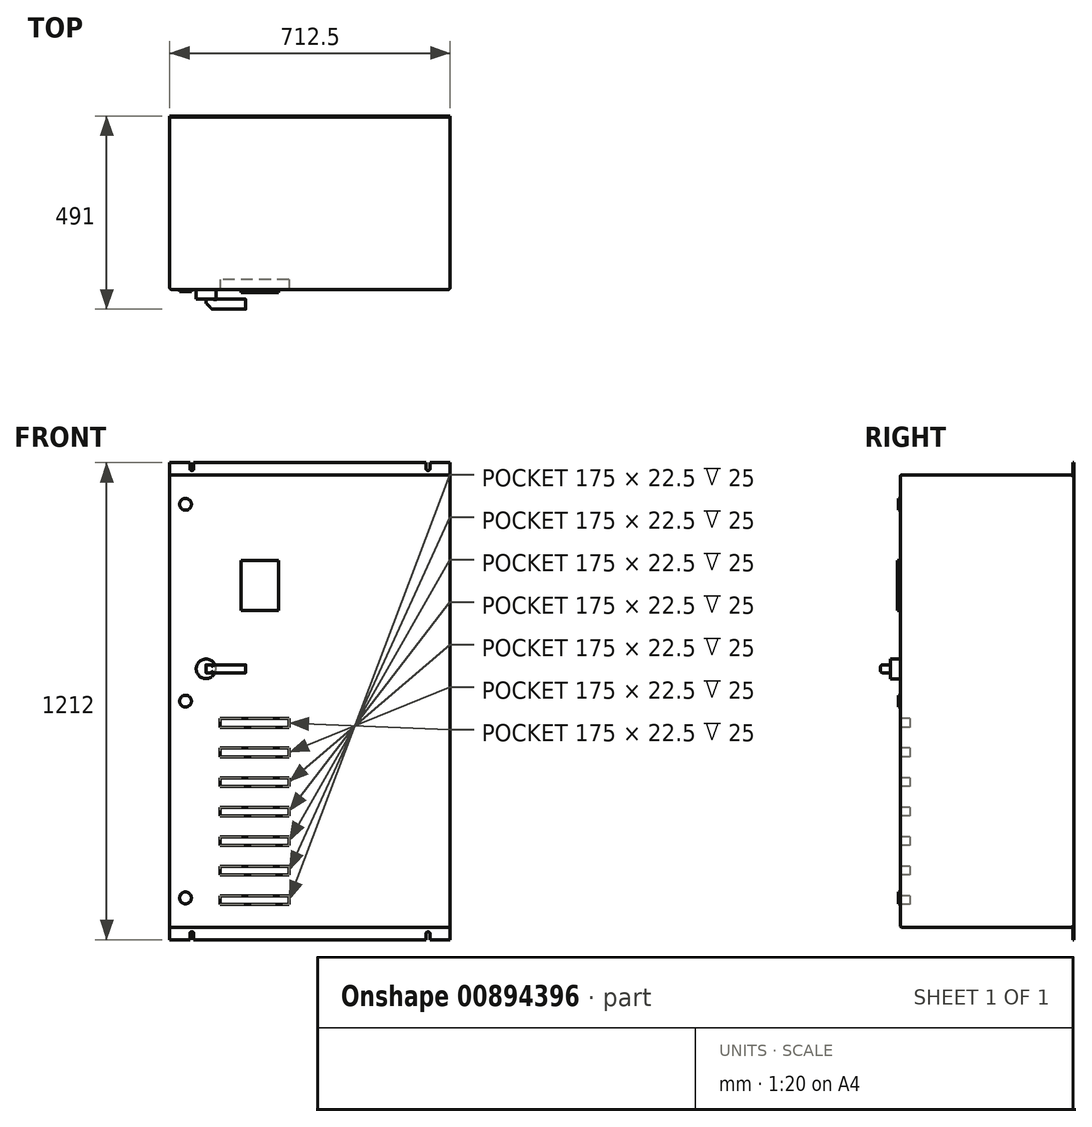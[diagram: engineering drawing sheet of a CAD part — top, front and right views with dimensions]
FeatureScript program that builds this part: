
annotation { "Feature Type Name" : "Feature", "Feature Type Description" : "" }
export const myFeature = defineFeature(function(context is Context, id is Id, definition is map)
    precondition{}
    {
        {
            var Q0;
            Q0=qCreatedBy(makeId("Front.planeOp"),FACE);
            var sketch = newSketch(context, id + "F0", { "sketchPlane" : qUnion([Q0])});
            skLineSegment(sketch, "E0.bottom", {"start": v(356.25, 575) * mm, "end": v(-356.25, 575) * mm});
            skLineSegment(sketch, "E0.top", {"start": v(356.25, -575) * mm, "end": v(-356.25, -575) * mm});
            skLineSegment(sketch, "E0.left", {"start": v(356.25, 575) * mm, "end": v(356.25, -575) * mm});
            skLineSegment(sketch, "E0.right", {"start": v(-356.25, 575) * mm, "end": v(-356.25, -575) * mm});
            skPoint(sketch, "E0.middle", {"position": v(0, 0) * mm});
            skSolve(sketch);
        }
        {
            var Q0;
            Q0 = qSketchRegion(id + "F0", true);
            extrude(context, id + "F1", {"entities" : qUnion([Q0]), "depth" : 438 * mm, "offsetDistance" : 25 * mm});
        }
        {
            var Q0;
            Q0=makeQuery(id+"F1.opExtrude","CAP_FACE",FACE,{"disambiguationData":[OSD([sQuery(id+"F0.wireOp",EDGE,"E0.bottom"),sQuery(id+"F0.wireOp",EDGE,"E0.top"),sQuery(id+"F0.wireOp",EDGE,"E0.left"),sQuery(id+"F0.wireOp",EDGE,"E0.right")])],"isStart":false});
            var sketch = newSketch(context, id + "F2", { "sketchPlane" : qUnion([Q0])});
            skCircle(sketch, "E1", {"center": v(-263.95, 82) * mm, "radius": 25 * mm});
            skSolve(sketch);
        }
        {
            var Q0;
            Q0 = qSketchRegion(id + "F2", true);
            extrude(context, id + "F3", {"entities" : qUnion([Q0]), "depth" : 25 * mm, "offsetDistance" : 25 * mm});
        }
        {
            var Q0;
            Q0=makeQuery(id+"F3.opExtrude","CAP_FACE",FACE,{"disambiguationData":[OSD([sQuery(id+"F2.wireOp",EDGE,"E1")])],"isStart":false});
            var sketch = newSketch(context, id + "F4", { "sketchPlane" : qUnion([Q0])});
            skLineSegment(sketch, "E2", {"start": v(-263.95, 82) * mm, "end": v(-263.95, 92) * mm});
            skLineSegment(sketch, "E3", {"start": v(-263.95, 92) * mm, "end": v(-163.46, 92) * mm});
            skLineSegment(sketch, "E4", {"start": v(-163.46, 92) * mm, "end": v(-163.46, 72) * mm});
            skLineSegment(sketch, "E5", {"start": v(-163.46, 72) * mm, "end": v(-263.95, 72) * mm});
            skLineSegment(sketch, "E6", {"start": v(-263.95, 72) * mm, "end": v(-263.95, 82) * mm});
            skSolve(sketch);
        }
        {
            var Q0;
            Q0 = qSketchRegion(id + "F4", true);
            extrude(context, id + "F5", {"entities" : qUnion([Q0]), "operationType" : NewBodyOperationType.ADD, "depth" : 25 * mm, "offsetDistance" : 25 * mm});
        }
        {
            var Q0;
            Q0=makeQuery(id+"F5.opExtrude","CAP_EDGE",EDGE,{"disambiguationData":[OSD([sQuery(id+"F4.wireOp",EDGE,"E2"),sQuery(id+"F4.wireOp",EDGE,"E6")])],"isStart":false});
            chamfer(context, id + "F6", {"entities" : qUnion([Q0]), "width" : 15 * mm, "tangentPropagation" : true});
        }
        {
            var Q0;
            {var subQ0=sQuery(id+"F4.wireOp",EDGE,"E5");Q0=makeQuery(id+"F5.boolean.opBoolean","SPLIT",EDGE,{"disambiguationData":[topologyDisambiguationEdgeConnected([makeQuery(id+"F3.opExtrude","CAP_FACE",FACE,{"disambiguationData":[OSD([sQuery(id+"F2.wireOp",EDGE,"E1")])],"isStart":false})])],"derivedFrom":makeQuery(id+"F5.opExtrude","CAP_EDGE",EDGE,{"disambiguationData":[OSD([subQ0])],"isStart":true})});}
            var Q1;
            Q1=makeQuery(id+"F5.opExtrude","CAP_EDGE",EDGE,{"disambiguationData":[OSD([sQuery(id+"F4.wireOp",EDGE,"E2"),sQuery(id+"F4.wireOp",EDGE,"E6")])],"isStart":true});
            var Q2;
            {var subQ0=sQuery(id+"F4.wireOp",EDGE,"E3");Q2=makeQuery(id+"F5.boolean.opBoolean","SPLIT",EDGE,{"disambiguationData":[topologyDisambiguationEdgeConnected([makeQuery(id+"F3.opExtrude","CAP_FACE",FACE,{"disambiguationData":[OSD([sQuery(id+"F2.wireOp",EDGE,"E1")])],"isStart":false})])],"derivedFrom":makeQuery(id+"F5.opExtrude","CAP_EDGE",EDGE,{"disambiguationData":[OSD([subQ0])],"isStart":true})});}
            var Q3;
            Q3=makeQuery(id+"F5.opExtrude","CAP_EDGE",EDGE,{"disambiguationData":[OSD([sQuery(id+"F4.wireOp",EDGE,"E3")])],"isStart":false});
            var Q4;
            Q4=makeQuery(id+"F5.opExtrude","CAP_EDGE",EDGE,{"disambiguationData":[OSD([sQuery(id+"F4.wireOp",EDGE,"E5")])],"isStart":false});
            var Q5;
            {var subQ0=sQuery(id+"F4.wireOp",EDGE,"E6");var subQ1=sQuery(id+"F4.wireOp",EDGE,"E2");Q5=makeQuery(id+"F6.opChamfer","BLEND_EDGE",EDGE,{"blendedFrom":[makeQuery(id+"F5.opExtrude","CAP_EDGE",EDGE,{"disambiguationData":[OSD([subQ1,subQ0])],"isStart":false}),makeQuery(id+"F5.opExtrude","CAP_FACE",FACE,{"disambiguationData":[OSD([subQ1,sQuery(id+"F4.wireOp",EDGE,"E3"),sQuery(id+"F4.wireOp",EDGE,"E4"),sQuery(id+"F4.wireOp",EDGE,"E5"),subQ0])],"isStart":false})],"blendedInto":[makeQuery(id+"F5.opExtrude","CAP_FACE",FACE,{"disambiguationData":[OSD([subQ1,sQuery(id+"F4.wireOp",EDGE,"E3"),sQuery(id+"F4.wireOp",EDGE,"E4"),sQuery(id+"F4.wireOp",EDGE,"E5"),subQ0])],"isStart":false})]});}
            var Q6;
            {var subQ0=sQuery(id+"F4.wireOp",EDGE,"E6");var subQ1=sQuery(id+"F4.wireOp",EDGE,"E2");Q6=makeQuery(id+"F6.opChamfer","BLEND_EDGE",EDGE,{"blendedFrom":[makeQuery(id+"F5.opExtrude","CAP_EDGE",EDGE,{"disambiguationData":[OSD([subQ1,subQ0])],"isStart":false}),makeQuery(id+"F5.opExtrude","SWEPT_FACE",FACE,{"disambiguationData":[OSD([subQ1,subQ0])]})],"blendedInto":[makeQuery(id+"F5.opExtrude","SWEPT_FACE",FACE,{"disambiguationData":[OSD([subQ1,subQ0])]})]});}
            fillet(context, id + "F7", {"entities" : qUnion([Q0, Q1, Q2, Q3, Q4, Q5, Q6]), "radius" : 5 * mm, "tangentPropagation" : true, "allowEdgeOverflow" : false});
        }
        {
            var Q0;
            Q0=makeQuery(id+"F1.opExtrude","CAP_FACE",FACE,{"disambiguationData":[OSD([sQuery(id+"F0.wireOp",EDGE,"E0.bottom"),sQuery(id+"F0.wireOp",EDGE,"E0.top"),sQuery(id+"F0.wireOp",EDGE,"E0.left"),sQuery(id+"F0.wireOp",EDGE,"E0.right")])],"isStart":true});
            var sketch = newSketch(context, id + "F8", { "sketchPlane" : qUnion([Q0])});
            skLineSegment(sketch, "E7.bottom", {"start": v(356.25, 606) * mm, "end": v(300, 606) * mm});
            skLineSegment(sketch, "E7.top", {"start": v(356.25, -606) * mm, "end": v(305, -606) * mm});
            skLineSegment(sketch, "E7.left", {"start": v(356.25, 606) * mm, "end": v(356.25, -606) * mm});
            skLineSegment(sketch, "E7.right", {"start": v(-356.25, 606) * mm, "end": v(-356.25, -606) * mm});
            skPoint(sketch, "E7.middle", {"position": v(0, 0) * mm});
            skLineSegment(sketch, "E8", {"start": v(0, 665.64) * mm, "end": v(0, -668.18) * mm, "construction": true});
            skLineSegment(sketch, "E9.bottom", {"start": v(300, 647.98) * mm, "end": v(-300, 647.98) * mm, "construction": true});
            skLineSegment(sketch, "E9.top", {"start": v(300, -647.98) * mm, "end": v(-300, -647.98) * mm, "construction": true});
            skLineSegment(sketch, "E9.left", {"start": v(300, 647.98) * mm, "end": v(300, -647.98) * mm, "construction": true});
            skLineSegment(sketch, "E9.right", {"start": v(-300, 647.98) * mm, "end": v(-300, -647.98) * mm, "construction": true});
            skLineSegment(sketch, "E10.left", {"start": v(-295, -606) * mm, "end": v(-295, -591) * mm});
            skLineSegment(sketch, "E10.right", {"start": v(-305, -606) * mm, "end": v(-305, -591) * mm});
            skPoint(sketch, "E10.middle", {"position": v(-300, -598.5) * mm});
            skArc(sketch, "E11", {"start": v(-305, -591) * mm, "mid": v(-300, -586) * mm, "end": v(-295, -591) * mm});
            skLineSegment(sketch, "E12.trimOffspring", {"start": v(-305, -606) * mm, "end": v(-356.25, -606) * mm});
            skLineSegment(sketch, "E13.MirrorCS", {"start": v(295, -606) * mm, "end": v(300, -606) * mm});
            skLineSegment(sketch, "E14.MirrorCS", {"start": v(305, -606) * mm, "end": v(305, -591) * mm});
            skLineSegment(sketch, "E15.MirrorCS", {"start": v(300, -606) * mm, "end": v(295, -606) * mm});
            skArc(sketch, "E16.MirrorCS", {"start": v(305, -591) * mm, "mid": v(300, -586) * mm, "end": v(295, -591) * mm});
            skLineSegment(sketch, "E17.MirrorCS", {"start": v(295, -606) * mm, "end": v(295, -591) * mm});
            skPoint(sketch, "E18.MirrorP", {"position": v(300, -598.5) * mm});
            skLineSegment(sketch, "E19.MirrorCS", {"start": v(-300, 606) * mm, "end": v(-305, 606) * mm});
            skLineSegment(sketch, "E20.MirrorCS", {"start": v(305, 606) * mm, "end": v(300, 606) * mm});
            skArc(sketch, "E21.MirrorCS", {"start": v(305, 591) * mm, "mid": v(300, 586) * mm, "end": v(295, 591) * mm});
            skLineSegment(sketch, "E22.MirrorCS", {"start": v(295, 606) * mm, "end": v(295, 591) * mm});
            skArc(sketch, "E23.MirrorCS", {"start": v(-305, 591) * mm, "mid": v(-300, 586) * mm, "end": v(-295, 591) * mm});
            skLineSegment(sketch, "E24.MirrorCS", {"start": v(-305, 606) * mm, "end": v(-305, 591) * mm});
            skLineSegment(sketch, "E25.MirrorCS", {"start": v(300, 606) * mm, "end": v(305, 606) * mm});
            skLineSegment(sketch, "E26.MirrorCS", {"start": v(-305, 606) * mm, "end": v(-300, 606) * mm});
            skLineSegment(sketch, "E27.MirrorCS", {"start": v(-295, 606) * mm, "end": v(-295, 591) * mm});
            skLineSegment(sketch, "E28.MirrorCS", {"start": v(305, 606) * mm, "end": v(305, 591) * mm});
            skPoint(sketch, "E29.MirrorP", {"position": v(300, 598.5) * mm});
            skPoint(sketch, "E30.MirrorP", {"position": v(-300, 598.5) * mm});
            skLineSegment(sketch, "E31.trimOffspring", {"start": v(300, -606) * mm, "end": v(-295, -606) * mm});
            skLineSegment(sketch, "E32.trimOffspring", {"start": v(295, 606) * mm, "end": v(-295, 606) * mm});
            skLineSegment(sketch, "E33.trimOffspring", {"start": v(-300, 606) * mm, "end": v(-356.25, 606) * mm});
            skPoint(sketch, "E34.orphan", {"position": v(-295, 606) * mm});
            skSolve(sketch);
        }
        {
            var Q0;
            Q0 = qSketchRegion(id + "F8", true);
            extrude(context, id + "F9", {"entities" : qUnion([Q0]), "operationType" : NewBodyOperationType.ADD, "depth" : 3 * mm, "offsetDistance" : 25 * mm});
        }
        {
            var Q0;
            Q0=makeQuery(id+"F1.opExtrude","CAP_FACE",FACE,{"disambiguationData":[OSD([sQuery(id+"F0.wireOp",EDGE,"E0.bottom"),sQuery(id+"F0.wireOp",EDGE,"E0.top"),sQuery(id+"F0.wireOp",EDGE,"E0.left"),sQuery(id+"F0.wireOp",EDGE,"E0.right")])],"isStart":false});
            var sketch = newSketch(context, id + "F10", { "sketchPlane" : qUnion([Q0])});
            skLineSegment(sketch, "E35.bottom", {"start": v(-79.36, 357.66) * mm, "end": v(-175.27, 357.66) * mm});
            skLineSegment(sketch, "E35.top", {"start": v(-79.36, 230.17) * mm, "end": v(-175.27, 230.17) * mm});
            skLineSegment(sketch, "E35.left", {"start": v(-79.36, 357.66) * mm, "end": v(-79.36, 230.17) * mm});
            skLineSegment(sketch, "E35.right", {"start": v(-175.27, 357.66) * mm, "end": v(-175.27, 230.17) * mm});
            skPoint(sketch, "E35.middle", {"position": v(-127.32, 293.91) * mm});
            skSolve(sketch);
        }
        {
            var Q0;
            Q0 = qSketchRegion(id + "F10", true);
            extrude(context, id + "F11", {"entities" : qUnion([Q0]), "depth" : 7.5 * mm, "offsetDistance" : 25 * mm});
        }
        {
            var Q0;
            Q0=makeQuery(id+"F1.opExtrude","CAP_FACE",FACE,{"disambiguationData":[OSD([sQuery(id+"F0.wireOp",EDGE,"E0.bottom"),sQuery(id+"F0.wireOp",EDGE,"E0.top"),sQuery(id+"F0.wireOp",EDGE,"E0.left"),sQuery(id+"F0.wireOp",EDGE,"E0.right")])],"isStart":false});
            var sketch = newSketch(context, id + "F12", { "sketchPlane" : qUnion([Q0])});
            skLineSegment(sketch, "E36.bottom", {"start": v(-53.17, -44.51) * mm, "end": v(-228.17, -44.51) * mm});
            skLineSegment(sketch, "E36.top", {"start": v(-53.17, -67.01) * mm, "end": v(-228.17, -67.01) * mm});
            skLineSegment(sketch, "E36.left", {"start": v(-53.17, -44.51) * mm, "end": v(-53.17, -67.01) * mm});
            skLineSegment(sketch, "E36.right", {"start": v(-228.17, -44.51) * mm, "end": v(-228.17, -67.01) * mm});
            skPoint(sketch, "E36.middle", {"position": v(-140.67, -55.76) * mm});
            skLineSegment(sketch, "E37.0.1.0", {"start": v(-53.17, -142.01) * mm, "end": v(-228.17, -142.01) * mm});
            skLineSegment(sketch, "E37.0.1.1", {"start": v(-53.17, -119.51) * mm, "end": v(-228.17, -119.51) * mm});
            skLineSegment(sketch, "E37.0.1.2", {"start": v(-53.17, -119.51) * mm, "end": v(-53.17, -142.01) * mm});
            skLineSegment(sketch, "E37.0.1.3", {"start": v(-228.17, -119.51) * mm, "end": v(-228.17, -142.01) * mm});
            skLineSegment(sketch, "E37.0.2.0", {"start": v(-53.17, -217.01) * mm, "end": v(-228.17, -217.01) * mm});
            skLineSegment(sketch, "E37.0.2.1", {"start": v(-53.17, -194.51) * mm, "end": v(-228.17, -194.51) * mm});
            skLineSegment(sketch, "E37.0.2.2", {"start": v(-53.17, -194.51) * mm, "end": v(-53.17, -217.01) * mm});
            skLineSegment(sketch, "E37.0.2.3", {"start": v(-228.17, -194.51) * mm, "end": v(-228.17, -217.01) * mm});
            skLineSegment(sketch, "E37.0.3.0", {"start": v(-53.17, -292.01) * mm, "end": v(-228.17, -292.01) * mm});
            skLineSegment(sketch, "E37.0.3.1", {"start": v(-53.17, -269.51) * mm, "end": v(-228.17, -269.51) * mm});
            skLineSegment(sketch, "E37.0.3.2", {"start": v(-53.17, -269.51) * mm, "end": v(-53.17, -292.01) * mm});
            skLineSegment(sketch, "E37.0.3.3", {"start": v(-228.17, -269.51) * mm, "end": v(-228.17, -292.01) * mm});
            skLineSegment(sketch, "E37.0.4.0", {"start": v(-53.17, -367.01) * mm, "end": v(-228.17, -367.01) * mm});
            skLineSegment(sketch, "E37.0.4.1", {"start": v(-53.17, -344.51) * mm, "end": v(-228.17, -344.51) * mm});
            skLineSegment(sketch, "E37.0.4.2", {"start": v(-53.17, -344.51) * mm, "end": v(-53.17, -367.01) * mm});
            skLineSegment(sketch, "E37.0.4.3", {"start": v(-228.17, -344.51) * mm, "end": v(-228.17, -367.01) * mm});
            skLineSegment(sketch, "E37.0.5.0", {"start": v(-53.17, -442.01) * mm, "end": v(-228.17, -442.01) * mm});
            skLineSegment(sketch, "E37.0.5.1", {"start": v(-53.17, -419.51) * mm, "end": v(-228.17, -419.51) * mm});
            skLineSegment(sketch, "E37.0.5.2", {"start": v(-53.17, -419.51) * mm, "end": v(-53.17, -442.01) * mm});
            skLineSegment(sketch, "E37.0.5.3", {"start": v(-228.17, -419.51) * mm, "end": v(-228.17, -442.01) * mm});
            skLineSegment(sketch, "E37.0.6.0", {"start": v(-53.17, -517.01) * mm, "end": v(-228.17, -517.01) * mm});
            skLineSegment(sketch, "E37.0.6.1", {"start": v(-53.17, -494.51) * mm, "end": v(-228.17, -494.51) * mm});
            skLineSegment(sketch, "E37.0.6.2", {"start": v(-53.17, -494.51) * mm, "end": v(-53.17, -517.01) * mm});
            skLineSegment(sketch, "E37.0.6.3", {"start": v(-228.17, -494.51) * mm, "end": v(-228.17, -517.01) * mm});
            skLineSegment(sketch, "E37.direction1", {"start": v(-228.17, -67.01) * mm, "end": v(-203.17, -67.01) * mm, "construction": true});
            skLineSegment(sketch, "E37.direction2", {"start": v(-228.17, -67.01) * mm, "end": v(-228.17, -142.01) * mm, "construction": true});
            skSolve(sketch);
        }
        {
            var Q0;
            Q0 = qSketchRegion(id + "F12", true);
            extrude(context, id + "F13", {"entities" : qUnion([Q0]), "operationType" : NewBodyOperationType.REMOVE, "oppositeDirection" : true, "depth" : 25 * mm, "offsetDistance" : 25 * mm});
        }
        {
            var Q0;
            Q0=makeQuery(id+"F1.opExtrude","SWEPT_EDGE",EDGE,{"disambiguationData":[OSD([sQuery(id+"F0.wireOp",EDGE,"E0.bottom"),sQuery(id+"F0.wireOp",EDGE,"E0.right")])]});
            var Q1;
            Q1=makeQuery(id+"F1.opExtrude","SWEPT_EDGE",EDGE,{"disambiguationData":[OSD([sQuery(id+"F0.wireOp",EDGE,"E0.bottom"),sQuery(id+"F0.wireOp",EDGE,"E0.left")])]});
            var Q2;
            Q2=makeQuery(id+"F1.opExtrude","CAP_EDGE",EDGE,{"disambiguationData":[OSD([sQuery(id+"F0.wireOp",EDGE,"E0.bottom")])],"isStart":false});
            var Q3;
            Q3=makeQuery(id+"F1.opExtrude","CAP_EDGE",EDGE,{"disambiguationData":[OSD([sQuery(id+"F0.wireOp",EDGE,"E0.left")])],"isStart":false});
            var Q4;
            Q4=makeQuery(id+"F1.opExtrude","CAP_EDGE",EDGE,{"disambiguationData":[OSD([sQuery(id+"F0.wireOp",EDGE,"E0.right")])],"isStart":false});
            var Q5;
            Q5=makeQuery(id+"F1.opExtrude","SWEPT_EDGE",EDGE,{"disambiguationData":[OSD([sQuery(id+"F0.wireOp",EDGE,"E0.top"),sQuery(id+"F0.wireOp",EDGE,"E0.right")])]});
            var Q6;
            Q6=makeQuery(id+"F1.opExtrude","CAP_EDGE",EDGE,{"disambiguationData":[OSD([sQuery(id+"F0.wireOp",EDGE,"E0.top")])],"isStart":false});
            var Q7;
            Q7=makeQuery(id+"F1.opExtrude","SWEPT_EDGE",EDGE,{"disambiguationData":[OSD([sQuery(id+"F0.wireOp",EDGE,"E0.top"),sQuery(id+"F0.wireOp",EDGE,"E0.left")])]});
            fillet(context, id + "F14", {"entities" : qUnion([Q0, Q1, Q2, Q3, Q4, Q5, Q6, Q7]), "radius" : 5 * mm, "tangentPropagation" : true, "allowEdgeOverflow" : false});
        }
        {
            var Q0;
            Q0=makeQuery(id+"F1.opExtrude","CAP_FACE",FACE,{"disambiguationData":[OSD([sQuery(id+"F0.wireOp",EDGE,"E0.bottom"),sQuery(id+"F0.wireOp",EDGE,"E0.top"),sQuery(id+"F0.wireOp",EDGE,"E0.left"),sQuery(id+"F0.wireOp",EDGE,"E0.right")])],"isStart":false});
            var sketch = newSketch(context, id + "F15", { "sketchPlane" : qUnion([Q0])});
            skCircle(sketch, "E38", {"center": v(-316.07, 0) * mm, "radius": 15 * mm});
            skPoint(sketch, "E38.centerSnap0", {"position": v(-351.25, 0) * mm});
            skCircle(sketch, "E39", {"center": v(-316.07, -500) * mm, "radius": 15 * mm});
            skCircle(sketch, "E40", {"center": v(-316.07, 500) * mm, "radius": 15 * mm});
            skSolve(sketch);
        }
        {
            var Q0;
            Q0 = qSketchRegion(id + "F15", true);
            extrude(context, id + "F16", {"entities" : qUnion([Q0]), "depth" : 5 * mm, "offsetDistance" : 25 * mm});
        }
    });
